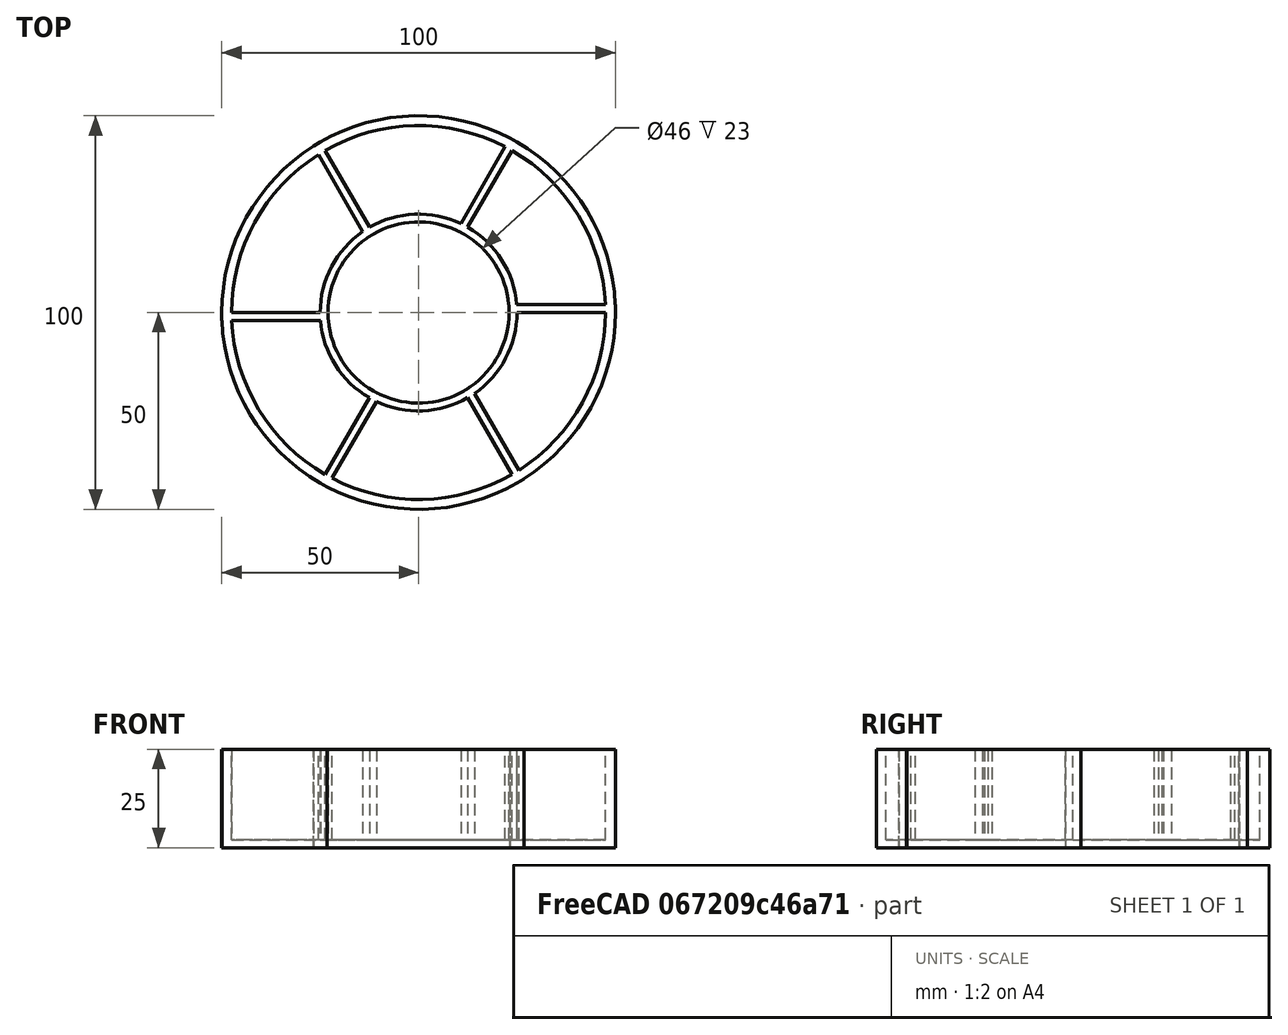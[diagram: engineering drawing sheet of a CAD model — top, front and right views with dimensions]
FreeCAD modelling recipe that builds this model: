
FCSTD DOCUMENT  (FreeCAD 0.20R29177 +426 (Git))
Label: first_230115
License: All rights reserved
LicenseURL: http://en.wikipedia.org/wiki/All_rights_reserved
objects: PartDesign::AdditiveBox×6, PartDesign::AdditiveCylinder×2, PartDesign::SubtractiveCylinder×2, PartDesign::Body×1
note: 21 computed .brp shape members not serialized (recipe doc carries the construction recipe); baked Part::Feature solids carry a one-line shape summary decoded from their .brp

FEATURE [PartDesign::AdditiveCylinder] Cylinder  label="main"
  Angle = 360
  AttacherType = Attacher::AttachEngine3D
  FirstAngle = 0
  Height = 25
  Radius = 50
  SecondAngle = 0
FEATURE [PartDesign::SubtractiveCylinder] Cylinder001  label="main_hole"
  Angle = 360
  AttacherType = Attacher::AttachEngine3D
  BaseFeature = -> Cylinder
  FirstAngle = 0
  Height = 23
  MapMode = 5
  Placement = pos=(0,0,25) rot=(0,1,0;3.14159rad)
  Radius = 47.5
  SecondAngle = 0
FEATURE [PartDesign::AdditiveBox] Box  label="sep_0"
  AttacherType = Attacher::AttachEngine3D
  BaseFeature = -> Cylinder001
  Height = 25
  Length = 50
  MapMode = 2
  Support = -> [X_Axis]
  Width = 2
FEATURE [PartDesign::AdditiveBox] Box001  label="sep_60"
  AttacherType = Attacher::AttachEngine3D
  AttachmentOffset = pos=(0,0,0) rot=(0,0,1;1.0472rad)
  BaseFeature = -> Box
  Height = 25
  Length = 50
  MapMode = 2
  Placement = pos=(0,0,0) rot=(0,0,1;1.0472rad)
  Support = -> [X_Axis]
  Width = 2
FEATURE [PartDesign::AdditiveBox] Box002  label="sep_120"
  AttacherType = Attacher::AttachEngine3D
  AttachmentOffset = pos=(0,0,0) rot=(0,0,1;2.0944rad)
  BaseFeature = -> Box001
  Height = 25
  Length = 50
  MapMode = 2
  Placement = pos=(0,0,0) rot=(0,0,1;2.0944rad)
  Support = -> [X_Axis]
  Width = 2
FEATURE [PartDesign::AdditiveBox] Box003  label="sep_180"
  AttacherType = Attacher::AttachEngine3D
  AttachmentOffset = pos=(0,0,0) rot=(0,0,1;3.14159rad)
  BaseFeature = -> Box002
  Height = 25
  Length = 50
  MapMode = 2
  Placement = pos=(0,0,0) rot=(0,0,1;3.14159rad)
  Support = -> [X_Axis]
  Width = 2
FEATURE [PartDesign::AdditiveBox] Box004  label="sep_240"
  AttacherType = Attacher::AttachEngine3D
  AttachmentOffset = pos=(0,0,0) rot=(0,0,1;4.18879rad)
  BaseFeature = -> Box003
  Height = 25
  Length = 50
  MapMode = 2
  Placement = pos=(0,0,0) rot=(0,0,1;4.18879rad)
  Support = -> [X_Axis]
  Width = 2
FEATURE [PartDesign::AdditiveBox] Box005  label="sep_300"
  AttacherType = Attacher::AttachEngine3D
  AttachmentOffset = pos=(0,0,0) rot=(0,0,1;5.23599rad)
  BaseFeature = -> Box004
  Height = 25
  Length = 50
  MapMode = 2
  Placement = pos=(0,0,0) rot=(0,0,1;5.23599rad)
  Support = -> [X_Axis]
  Width = 2
FEATURE [PartDesign::AdditiveCylinder] Cylinder002  label="center"
  Angle = 360
  AttacherType = Attacher::AttachEngine3D
  BaseFeature = -> Box005
  FirstAngle = 0
  Height = 25
  MapMode = 5
  Radius = 25
  SecondAngle = 0
  Support = -> [XY_Plane]
FEATURE [PartDesign::SubtractiveCylinder] Cylinder003
  Angle = 360
  AttacherType = Attacher::AttachEngine3D
  AttachmentOffset = pos=(0,0,2) rot=(0,0,1;0rad)
  BaseFeature = -> Cylinder002
  FirstAngle = 0
  Height = 23
  MapMode = 5
  Placement = pos=(0,0,2) rot=(0,0,1;0rad)
  Radius = 23
  SecondAngle = 0
  Support = -> [XY_Plane]
FEATURE [PartDesign::Body] Body
  Group = -> [Cylinder,Cylinder001,Box,Box001,Box002,Box003,Box004,Box005,Cylinder002,Cylinder003]
  Origin = -> Origin
  Tip = -> Cylinder003
